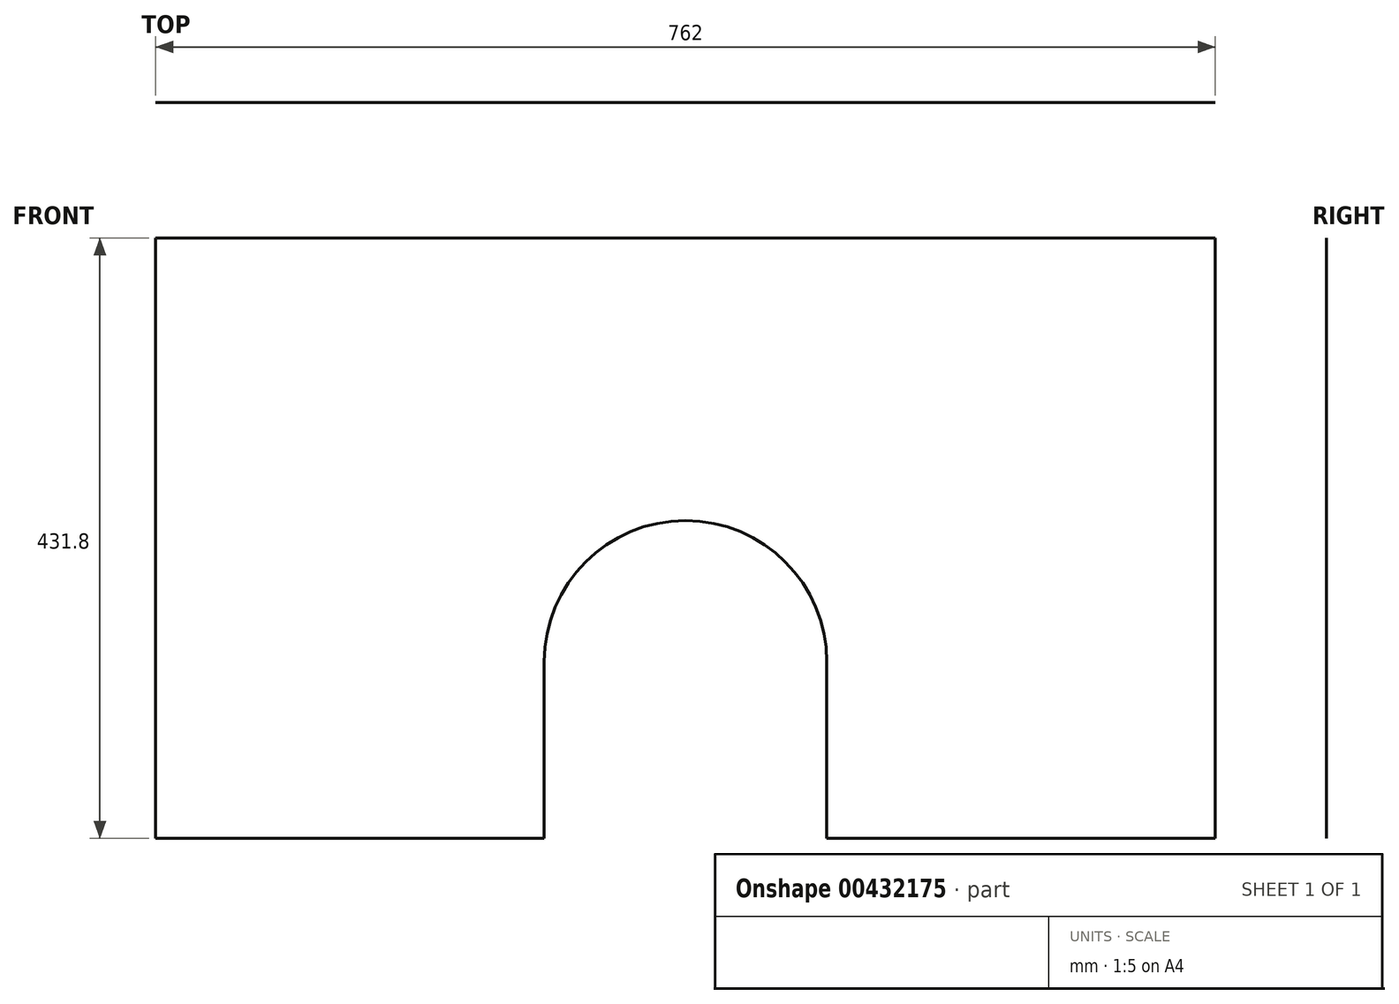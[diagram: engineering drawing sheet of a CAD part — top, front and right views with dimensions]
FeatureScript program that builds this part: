
annotation { "Feature Type Name" : "Feature", "Feature Type Description" : "" }
export const myFeature = defineFeature(function(context is Context, id is Id, definition is map)
    precondition{}
    {
        {
            var Q0;
            Q0=qCreatedBy(makeId("Front.planeOp"),FACE);
            var sketch = newSketch(context, id + "F0", { "sketchPlane" : qUnion([Q0])});
            skLineSegment(sketch, "E0.bottom", {"start": v(381, 215.9) * mm, "end": v(-381, 215.9) * mm});
            skLineSegment(sketch, "E0.top", {"start": v(381, -215.9) * mm, "end": v(101.6, -215.9) * mm});
            skLineSegment(sketch, "E0.left", {"start": v(381, 215.9) * mm, "end": v(381, -215.9) * mm});
            skLineSegment(sketch, "E0.right", {"start": v(-381, 215.9) * mm, "end": v(-381, -215.9) * mm});
            skPoint(sketch, "E0.middle", {"position": v(0, 0) * mm});
            skLineSegment(sketch, "E1", {"start": v(-101.6, -215.9) * mm, "end": v(-101.6, -88.9) * mm});
            skLineSegment(sketch, "E2", {"start": v(101.6, -215.9) * mm, "end": v(101.6, -88.9) * mm});
            skArc(sketch, "E3", {"start": v(101.6, -88.9) * mm, "mid": v(0, 12.7) * mm, "end": v(-101.6, -88.9) * mm});
            skLineSegment(sketch, "E4.trimOffspring", {"start": v(-101.6, -215.9) * mm, "end": v(-381, -215.9) * mm});
            skSolve(sketch);
        }
        {
            var Q0;
            Q0=makeQuery(id+"F0.imprint","IMPRINT",FACE,{"disambiguationData":[TD([[makeQuery(id+"F0.imprint","IMPRINT",EDGE,{"derivedFrom":sQuery(id+"F0.wireOp",EDGE,"E0.bottom")}),1.0]])]});
            extrude(context, id + "F1", {"entities" : qUnion([Q0]), "depth" : 1 / 203.2 * mm});
        }
    });
